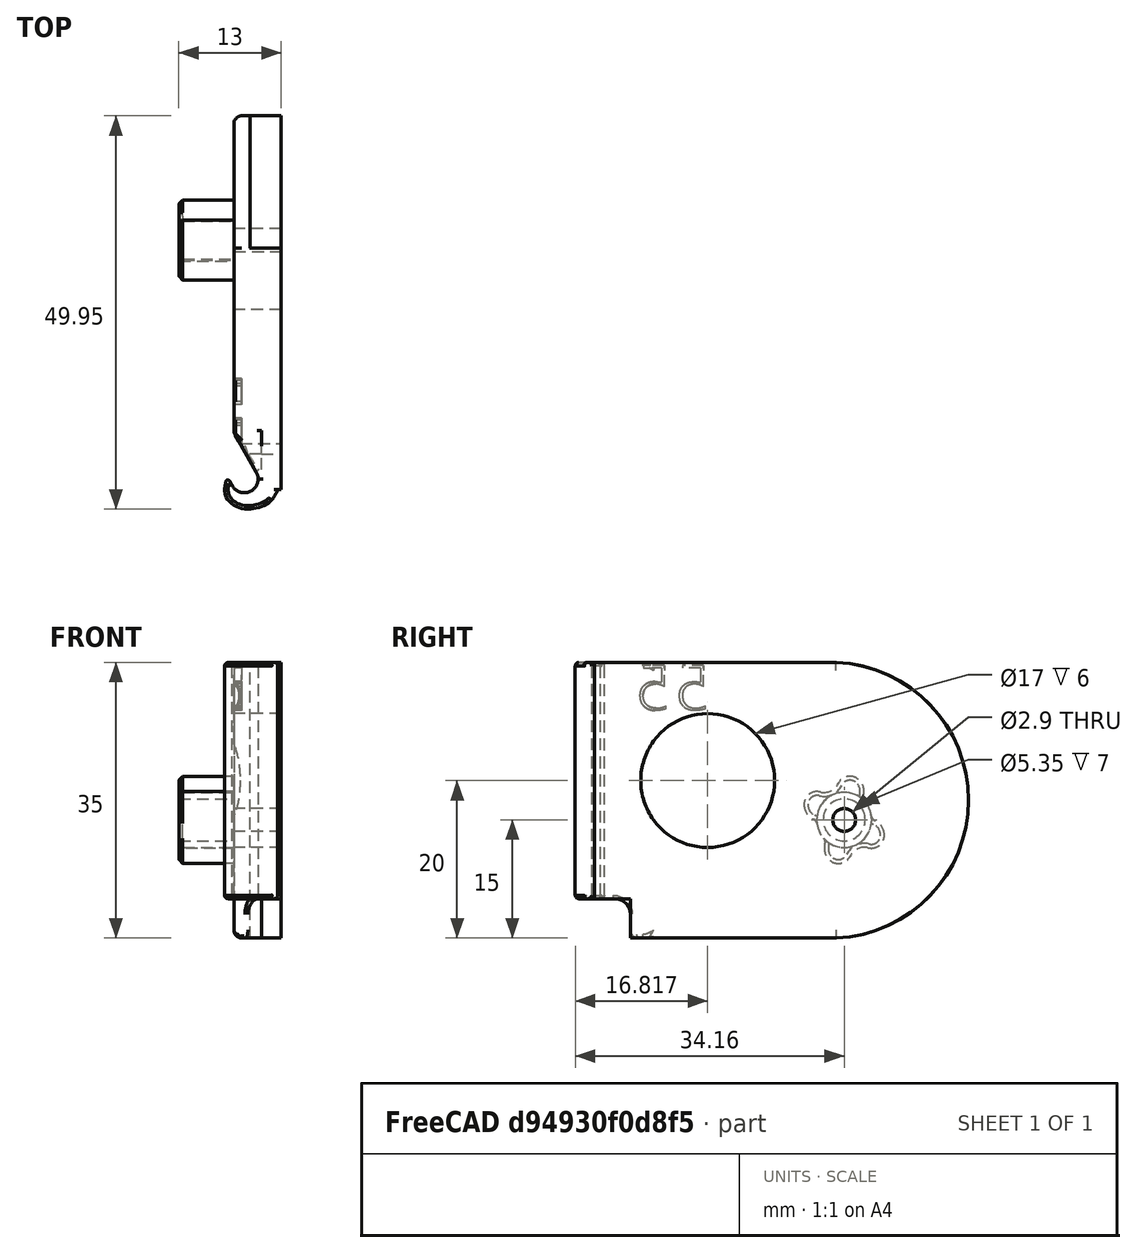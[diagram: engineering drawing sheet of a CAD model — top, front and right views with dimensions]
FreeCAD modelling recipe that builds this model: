
FCSTD DOCUMENT  (FreeCAD 0.18R)
Label: hinge-left-155deg-flat
License: All rights reserved
LicenseURL: http://en.wikipedia.org/wiki/All_rights_reserved
objects: App::FeaturePython×4, Part::FeaturePython×2, Part::Part2DObjectPython×1, Part::Extrusion×1, Part::Cut×1
note: 5 computed .brp shape members not serialized (recipe doc carries the construction recipe); baked Part::Feature solids carry a one-line shape summary decoded from their .brp

FEATURE [Part::FeaturePython] pillar_base_001  label="pillar-base_001"  # a2plus imported part (geometry in sourceFile) (typed FeaturePython)
  Placement = pos=(0.000608724,-0.00261462,0.00477004) rot=(1,0,0;6.28301rad)
  a2p_Version = V0.1
  fixedPosition = false
  objectType = a2pPart
  sourceFile = ./parts/pillar-base.fcstd
  subassemblyImport = false
  timeLastImport = 1.60452e+09
  updateColors = true
FEATURE [Part::Part2DObjectPython] ShapeString  # Draft 2D object (typed FeaturePython)
  FontFile = <path>
  Placement = pos=(1.61,10.5,29) rot=(0.57735,-0.57735,-0.57735;2.0944rad)
  Size = 6
  String = 55
  Tracking = 0
FEATURE [Part::Extrusion] Extrude
  Base = -> ShapeString
  Dir = (-1,-1e-16,2e-16)
  DirMode = 2
  FaceMakerClass = Part::FaceMakerBullseye
  LengthFwd = 2
  LengthRev = 0
  Solid = false
  Symmetric = false
FEATURE [Part::FeaturePython] bracket_left_flat_001  label="bracket-left-flat_001"  # a2plus imported part (geometry in sourceFile) (typed FeaturePython)
  a2p_Version = V0.1
  fixedPosition = true
  objectType = a2pPart
  sourceFile = ./parts/bracket-left-flat.fcstd
  subassemblyImport = false
  timeLastImport = 1.60454e+09
  updateColors = true
FEATURE [App::FeaturePython] axisCoincident_001  label="axisCoincident_001__bracket-left-flat_001"  # a2plus constraint (typed FeaturePython)
  Object1 = pillar_base_001
  Object2 = bracket_left_flat_001
  ParentTreeObject = -> pillar_base_001
  SubElement1 = Face17
  SubElement2 = Face48
  Suppressed = false
  Type = axial
  directionConstraint = 1
  lockRotation = false
FEATURE [App::FeaturePython] axisCoincident_001_mirror  label="axisCoincident_001__pillar-base_001"  # a2plus constraint (typed FeaturePython)
  Object1 = pillar_base_001
  Object2 = bracket_left_flat_001
  ParentTreeObject = -> bracket_left_flat_001
  SubElement1 = Face17
  SubElement2 = Face48
  Suppressed = false
  Type = axial
  directionConstraint = 1
  lockRotation = false
FEATURE [App::FeaturePython] planeCoincident_001  label="planeCoincident_001__bracket-left-flat_001"  # a2plus constraint (typed FeaturePython)
  Object1 = pillar_base_001
  Object2 = bracket_left_flat_001
  ParentTreeObject = -> pillar_base_001
  SubElement1 = Face1
  SubElement2 = Face72
  Suppressed = false
  Type = plane
  directionConstraint = 0
  offset = 0
FEATURE [App::FeaturePython] planeCoincident_001_mirror  label="planeCoincident_001__pillar-base_001"  # a2plus constraint (typed FeaturePython)
  Object1 = pillar_base_001
  Object2 = bracket_left_flat_001
  ParentTreeObject = -> bracket_left_flat_001
  SubElement1 = Face1
  SubElement2 = Face72
  Suppressed = false
  Type = plane
  directionConstraint = 0
  offset = 0
FEATURE [Part::Cut] Cut
  Base = -> bracket_left_flat_001
  Tool = -> Extrude
note: 1 file-system path scrubbed to <path> (originals preserved in the JSON sidecar)
